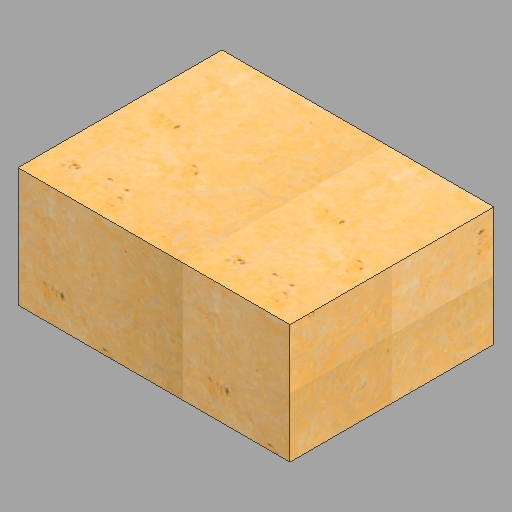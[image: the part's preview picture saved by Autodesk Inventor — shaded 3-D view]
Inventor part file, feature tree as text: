
AUTODESK INVENTOR PART (.ipt)
format: ipt  version: 2023 (Build 270158000, 158)  size: 360,960 bytes
history: native  units: in
note: dims shown in document units (in); Inventor stores cm internally (conversion verified against a paired STEP export)
features: extrude x1, sketch x1
ambient origin geometry x8: Origin, YZ Plane, XZ Plane, XY Plane, X Axis, Y Axis, Z Axis, Center Point
bodies: Solid1 (feature_tree)
feature tree (2):
  extrude  "Extrusion1"  Depth=36.0in
  sketch  "Sketch1"  dims[d0=21.0in d1=36.0in d2=48.0in d3=0.0in]
